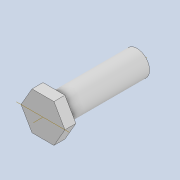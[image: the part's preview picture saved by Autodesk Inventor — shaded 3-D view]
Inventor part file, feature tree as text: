
AUTODESK INVENTOR PART (.ipt)
format: ipt  version: 2021 (Build 250183000, 183)  size: 96,256 bytes
history: native  units: mm
features: sketch x2, revolve x1, extrude x1, projected_geometry x1
ambient origin geometry x8: Origin, YZ Plane, XZ Plane, XY Plane, X Axis, Y Axis, Z Axis, Center Point
bodies: Solid1 (feature_tree)
feature tree (5):
  revolve  "Revolution1"  [1 undecoded]
  extrude  "Extrusion1"  Depth=7.0mm
  sketch  "Sketch1"  dims[d0=3.5mm d1=4.0mm]
  sketch  "Sketch2"  dims[d2=30.0mm d3=7.0mm d4=90.0deg d5=10.0mm d6=0.0mm]
  projected_geometry  "Projected Loop1"
note: 1 required parameter value undecoded (feature->parameter linkage not recoverable at this tier; creation-order binding heuristic only, values carry confidence <= 0.55)
